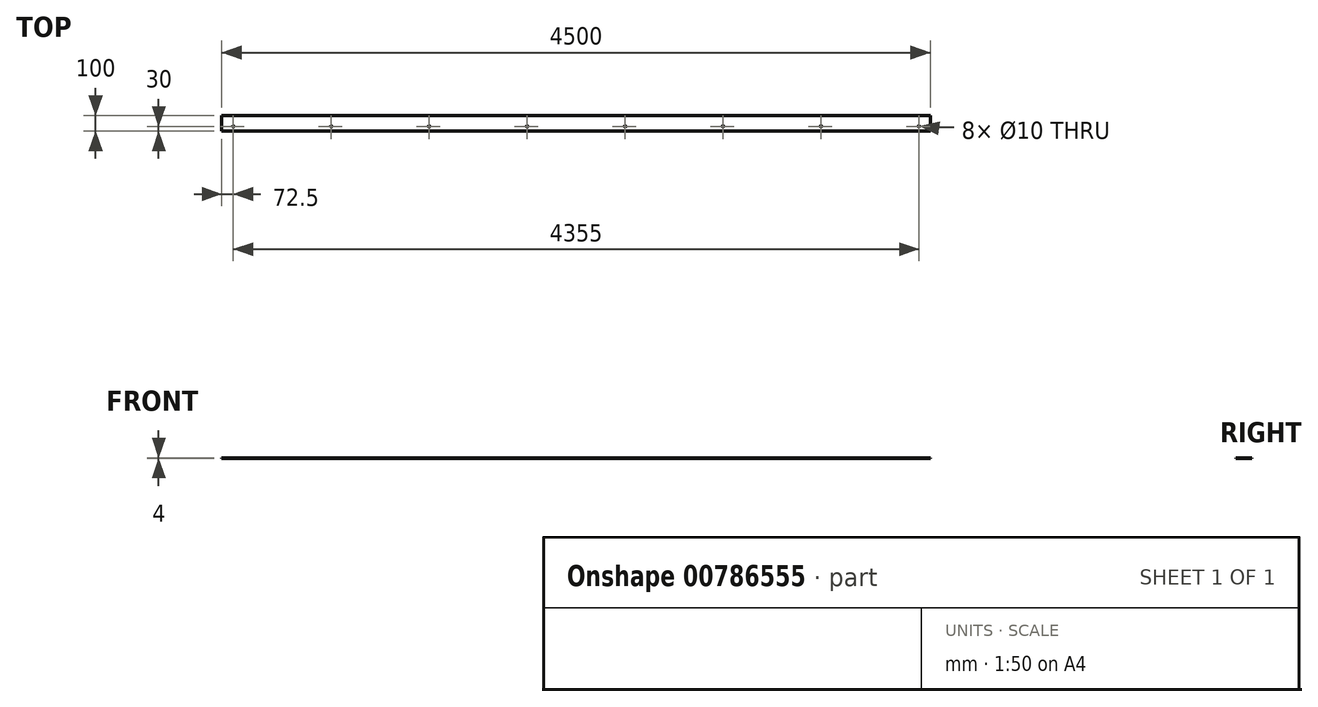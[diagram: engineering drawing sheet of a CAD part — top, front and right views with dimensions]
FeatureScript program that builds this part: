
annotation { "Feature Type Name" : "Feature", "Feature Type Description" : "" }
export const myFeature = defineFeature(function(context is Context, id is Id, definition is map)
    precondition{}
    {
        {
            var Q0;
            Q0=qCreatedBy(makeId("Top.planeOp"),FACE);
            var sketch = newSketch(context, id + "F0", { "sketchPlane" : qUnion([Q0])});
            skLineSegment(sketch, "E0.bottom", {"start": v(2250, 50) * mm, "end": v(-2250, 50) * mm});
            skLineSegment(sketch, "E0.top", {"start": v(2250, -50) * mm, "end": v(-2250, -50) * mm});
            skLineSegment(sketch, "E0.left", {"start": v(2250, 50) * mm, "end": v(2250, -50) * mm});
            skLineSegment(sketch, "E0.right", {"start": v(-2250, 50) * mm, "end": v(-2250, -50) * mm});
            skPoint(sketch, "E0.middle", {"position": v(0, 0) * mm});
            skCircle(sketch, "E1", {"center": v(-2177.5, -20) * mm, "radius": 5 * mm});
            skCircle(sketch, "E2", {"center": v(2177.5, -20) * mm, "radius": 5 * mm});
            skCircle(sketch, "E3.1.0.0", {"center": v(1555.36, -20) * mm, "radius": 5 * mm});
            skCircle(sketch, "E3.2.0.0", {"center": v(933.22, -20) * mm, "radius": 5 * mm});
            skCircle(sketch, "E3.3.0.0", {"center": v(311.08, -20) * mm, "radius": 5 * mm});
            skCircle(sketch, "E3.4.0.0", {"center": v(-311.06, -20) * mm, "radius": 5 * mm});
            skCircle(sketch, "E3.5.0.0", {"center": v(-933.2, -20) * mm, "radius": 5 * mm});
            skCircle(sketch, "E3.6.0.0", {"center": v(-1555.34, -20) * mm, "radius": 5 * mm});
            skLineSegment(sketch, "E3.direction1", {"start": v(2177.5, -20) * mm, "end": v(1555.36, -20) * mm, "construction": true});
            skSolve(sketch);
        }
        {
            var Q0;
            Q0=makeQuery(id+"F0.imprint","IMPRINT",FACE,{"disambiguationData":[TD([[makeQuery(id+"F0.imprint","IMPRINT",EDGE,{"derivedFrom":sQuery(id+"F0.wireOp",EDGE,"E0.bottom")}),1.0]])]});
            extrude(context, id + "F1", {"entities" : qUnion([Q0]), "depth" : 4 * mm, "offsetDistance" : 25 * mm});
        }
    });
